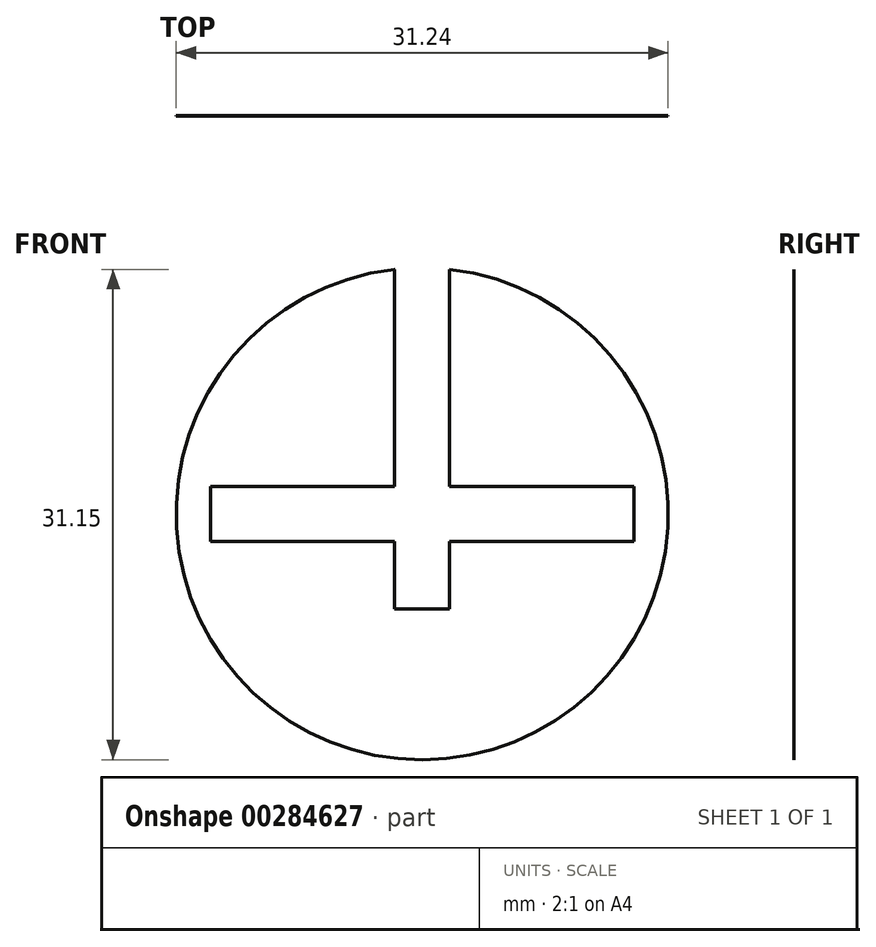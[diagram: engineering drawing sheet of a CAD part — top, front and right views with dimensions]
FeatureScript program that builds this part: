
annotation { "Feature Type Name" : "Feature", "Feature Type Description" : "" }
export const myFeature = defineFeature(function(context is Context, id is Id, definition is map)
    precondition{}
    {
        {
            var Q0;
            Q0=qCreatedBy(makeId("Front.planeOp"),FACE);
            var sketch = newSketch(context, id + "F0", { "sketchPlane" : qUnion([Q0])});
            skCircle(sketch, "E0", {"center": v(0, 0) * mm, "radius": 15.62 * mm});
            skLineSegment(sketch, "E1.bottom", {"start": v(13.45, -1.75) * mm, "end": v(-13.45, -1.75) * mm});
            skLineSegment(sketch, "E1.top", {"start": v(13.45, 1.75) * mm, "end": v(-13.45, 1.75) * mm});
            skLineSegment(sketch, "E1.left", {"start": v(13.45, -1.75) * mm, "end": v(13.45, 1.75) * mm});
            skLineSegment(sketch, "E1.right", {"start": v(-13.45, -1.75) * mm, "end": v(-13.45, 1.75) * mm});
            skLineSegment(sketch, "E2.bottom", {"start": v(-1.76, -6.06) * mm, "end": v(1.74, -6.06) * mm});
            skLineSegment(sketch, "E2.top", {"start": v(-1.76, 15.53) * mm, "end": v(1.74, 15.53) * mm});
            skLineSegment(sketch, "E2.left", {"start": v(-1.76, -6.06) * mm, "end": v(-1.76, 15.53) * mm});
            skLineSegment(sketch, "E2.right", {"start": v(1.74, -6.06) * mm, "end": v(1.74, 15.53) * mm});
            skPoint(sketch, "E3", {"position": v(-0.01, -6.06) * mm});
            skSolve(sketch);
        }
        {
            var Q0;
            {var subQ0=sQuery(id+"F0.wireOp",EDGE,"E2.top");var subQ1=sQuery(id+"F0.wireOp",EDGE,"E0");var subQ2=makeQuery(id+"F0.imprint","INTERSECT",VERTEX,{"derivedFrom":[subQ1,subQ0]});Q0=makeQuery(id+"F0.imprint","IMPRINT",FACE,{"disambiguationData":[TD([[makeQuery(id+"F0.imprint","IMPRINT",EDGE,{"disambiguationData":[TD([[subQ2,-1.0]])],"derivedFrom":subQ1}),-1.0]])]});}
            var Q1;
            {var subQ2=sQuery(id+"F0.wireOp",EDGE,"E1.left");Q1=makeQuery(id+"F0.imprint","IMPRINT",FACE,{"disambiguationData":[TD([[makeQuery(id+"F0.imprint","IMPRINT",EDGE,{"derivedFrom":subQ2}),-1.0]])]});}
            extrude(context, id + "F1", {"entities" : qUnion([Q0, Q1]), "depth" : 1 / 203.2 * mm});
        }
    });
